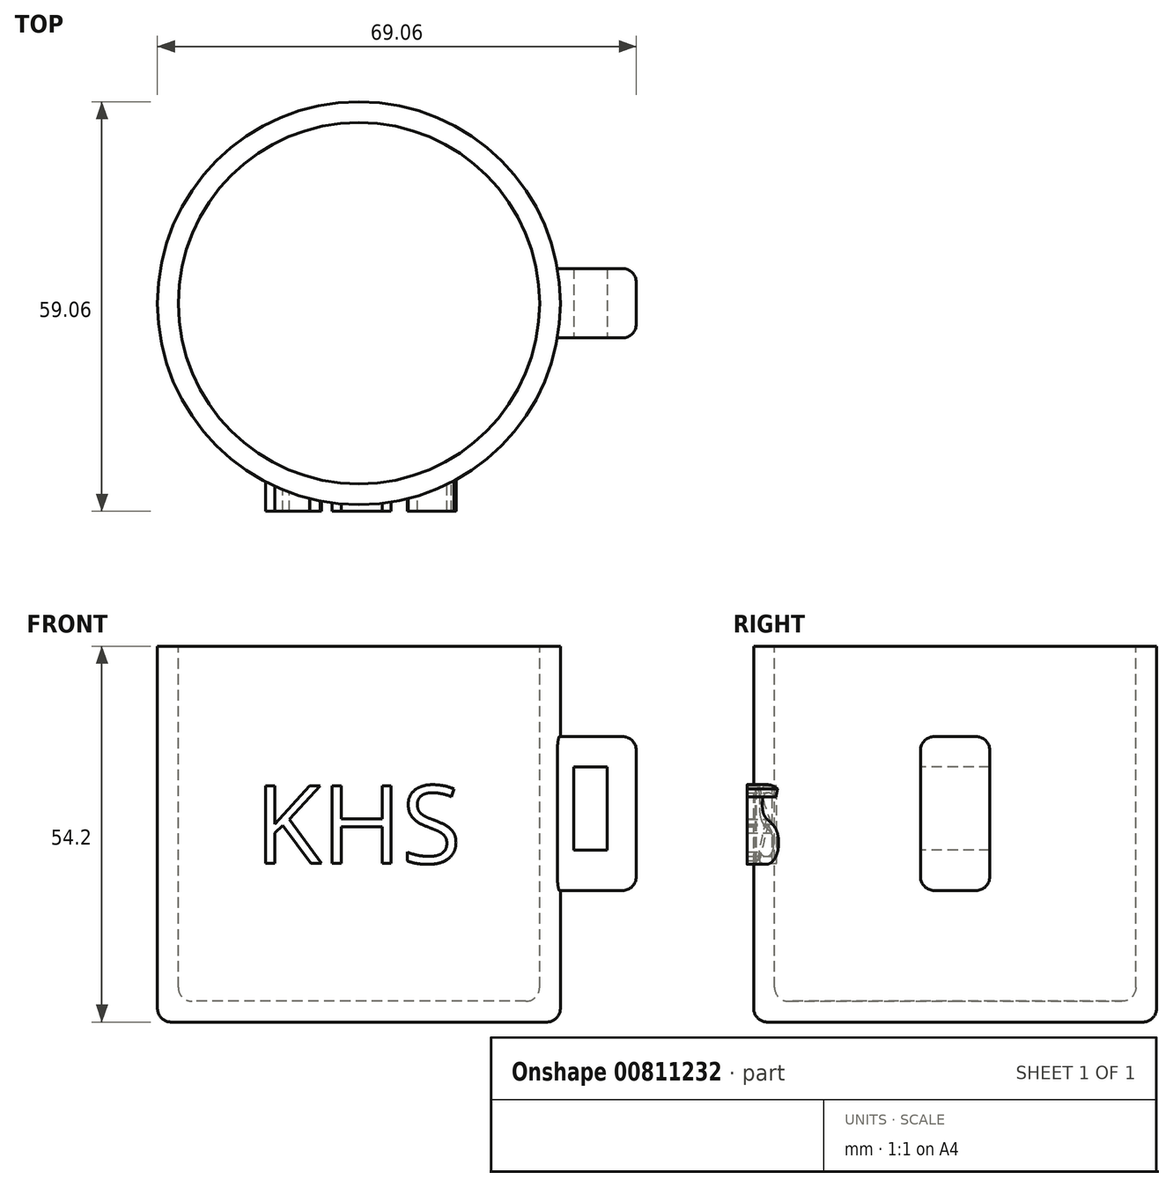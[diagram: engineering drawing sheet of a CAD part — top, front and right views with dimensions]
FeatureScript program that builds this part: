
annotation { "Feature Type Name" : "Feature", "Feature Type Description" : "" }
export const myFeature = defineFeature(function(context is Context, id is Id, definition is map)
    precondition{}
    {
        {
            var Q0;
            Q0=qCreatedBy(makeId("Front.planeOp"),FACE);
            var sketch = newSketch(context, id + "F0", { "sketchPlane" : qUnion([Q0])});
            skLineSegment(sketch, "E0", {"start": v(0, 41.97) * mm, "end": v(0, -44.14) * mm});
            skLineSegment(sketch, "E1", {"start": v(-6.15, -31.18) * mm, "end": v(24.06, -31.18) * mm});
            skLineSegment(sketch, "E2", {"start": v(26.06, -29.18) * mm, "end": v(26.06, 23.22) * mm});
            skLineSegment(sketch, "E3.0", {"start": v(29.06, -32.18) * mm, "end": v(29.06, 23.22) * mm});
            skLineSegment(sketch, "E3.1", {"start": v(-6.15, -34.18) * mm, "end": v(27.06, -34.18) * mm});
            skPoint(sketch, "E4.visualSharp", {"position": v(26.06, -31.18) * mm});
            skArc(sketch, "E4.filletArc", {"start": v(24.06, -31.18) * mm, "mid": v(25.48, -30.6) * mm, "end": v(26.06, -29.18) * mm});
            skPoint(sketch, "E5.visualSharp", {"position": v(29.06, -34.18) * mm});
            skArc(sketch, "E5.filletArc", {"start": v(27.06, -34.18) * mm, "mid": v(28.48, -33.6) * mm, "end": v(29.06, -32.18) * mm});
            skLineSegment(sketch, "E6", {"start": v(22.31, 20.02) * mm, "end": v(32.92, 20.02) * mm});
            skSolve(sketch);
        }
        {
            var Q0;
            {var subQ4=sQuery(id+"F0.wireOp",EDGE,"E4.filletArc");Q0=makeQuery(id+"F0.imprint","IMPRINT",FACE,{"disambiguationData":[TD([[makeQuery(id+"F0.imprint","IMPRINT",EDGE,{"derivedFrom":subQ4}),-1.0]])]});}
            var Q1;
            Q1=sQuery(id+"F0.wireOp",EDGE,"E0");
            revolve(context, id + "F1", {"surfaceOperationType" : NewSurfaceOperationType.NEW, "entities" : qUnion([Q0]), "axis" : qUnion([Q1]), "revolveType" : RevolveType.FULL});
        }
        {
            var Q0;
            Q0=qCreatedBy(makeId("Right.planeOp"),FACE);
            var sketch = newSketch(context, id + "F2", { "sketchPlane" : qUnion([Q0])});
            skLineSegment(sketch, "E7.bottom", {"start": v(-5, 7) * mm, "end": v(5, 7) * mm});
            skLineSegment(sketch, "E7.top", {"start": v(-5, -15.2) * mm, "end": v(5, -15.2) * mm});
            skLineSegment(sketch, "E7.left", {"start": v(-5, 7) * mm, "end": v(-5, -15.2) * mm});
            skLineSegment(sketch, "E7.right", {"start": v(5, 7) * mm, "end": v(5, -15.2) * mm});
            skSolve(sketch);
        }
        {
            var Q0;
            Q0=makeQuery(id+"F2.imprint","IMPRINT",FACE,{"disambiguationData":[TD([[makeQuery(id+"F2.imprint","IMPRINT",EDGE,{"derivedFrom":sQuery(id+"F2.wireOp",EDGE,"E7.bottom")}),-1.0]])]});
            extrude(context, id + "F3", {"entities" : qUnion([Q0]), "operationType" : NewBodyOperationType.ADD, "depth" : 40 * mm, "offsetDistance" : 25 * mm});
        }
        {
            var Q0;
            {var subQ0=sQuery(id+"F2.wireOp",EDGE,"E7.left");var subQ1=sQuery(id+"F2.wireOp",EDGE,"E7.bottom");Q0=makeQuery(id+"F3.boolean.opBoolean","SPLIT",EDGE,{"disambiguationData":[TD([makeQuery(id+"F1.opRevolve","SWEPT_FACE",FACE,{"disambiguationData":[OSD([sQuery(id+"F0.wireOp",EDGE,"E3.0")])]})])],"derivedFrom":makeQuery(id+"F3.opExtrude","SWEPT_EDGE",EDGE,{"disambiguationData":[OSD([subQ1,subQ0])]})});}
            var Q1;
            Q1=makeQuery(id+"F3.opExtrude","CAP_EDGE",EDGE,{"disambiguationData":[OSD([sQuery(id+"F2.wireOp",EDGE,"E7.bottom")])],"isStart":false});
            var Q2;
            Q2=makeQuery(id+"F3.opExtrude","CAP_EDGE",EDGE,{"disambiguationData":[OSD([sQuery(id+"F2.wireOp",EDGE,"E7.left")])],"isStart":false});
            var Q3;
            {var subQ0=sQuery(id+"F2.wireOp",EDGE,"E7.left");var subQ1=sQuery(id+"F2.wireOp",EDGE,"E7.top");Q3=makeQuery(id+"F3.boolean.opBoolean","SPLIT",EDGE,{"disambiguationData":[TD([makeQuery(id+"F1.opRevolve","SWEPT_FACE",FACE,{"disambiguationData":[OSD([sQuery(id+"F0.wireOp",EDGE,"E3.0")])]})])],"derivedFrom":makeQuery(id+"F3.opExtrude","SWEPT_EDGE",EDGE,{"disambiguationData":[OSD([subQ1,subQ0])]})});}
            var Q4;
            Q4=makeQuery(id+"F3.opExtrude","CAP_EDGE",EDGE,{"disambiguationData":[OSD([sQuery(id+"F2.wireOp",EDGE,"E7.top")])],"isStart":false});
            var Q5;
            Q5=makeQuery(id+"F3.opExtrude","CAP_EDGE",EDGE,{"disambiguationData":[OSD([sQuery(id+"F2.wireOp",EDGE,"E7.right")])],"isStart":false});
            var Q6;
            {var subQ0=sQuery(id+"F2.wireOp",EDGE,"E7.bottom");var subQ1=sQuery(id+"F2.wireOp",EDGE,"E7.right");Q6=makeQuery(id+"F3.boolean.opBoolean","SPLIT",EDGE,{"disambiguationData":[TD([makeQuery(id+"F1.opRevolve","SWEPT_FACE",FACE,{"disambiguationData":[OSD([sQuery(id+"F0.wireOp",EDGE,"E3.0")])]})])],"derivedFrom":makeQuery(id+"F3.opExtrude","SWEPT_EDGE",EDGE,{"disambiguationData":[OSD([subQ0,subQ1])]})});}
            var Q7;
            {var subQ0=sQuery(id+"F2.wireOp",EDGE,"E7.right");var subQ1=sQuery(id+"F2.wireOp",EDGE,"E7.top");Q7=makeQuery(id+"F3.boolean.opBoolean","SPLIT",EDGE,{"disambiguationData":[TD([makeQuery(id+"F1.opRevolve","SWEPT_FACE",FACE,{"disambiguationData":[OSD([sQuery(id+"F0.wireOp",EDGE,"E3.0")])]})])],"derivedFrom":makeQuery(id+"F3.opExtrude","SWEPT_EDGE",EDGE,{"disambiguationData":[OSD([subQ1,subQ0])]})});}
            fillet(context, id + "F4", {"entities" : qUnion([Q0, Q1, Q2, Q3, Q4, Q5, Q6, Q7]), "radius" : 2 * mm, "tangentPropagation" : true, "allowEdgeOverflow" : false});
        }
        {
            var Q0;
            {var subQ1=sQuery(id+"F2.wireOp",EDGE,"E7.left");Q0=makeQuery(id+"F3.boolean.opBoolean","SPLIT",FACE,{"disambiguationData":[TD([makeQuery(id+"F1.opRevolve","SWEPT_FACE",FACE,{"disambiguationData":[OSD([sQuery(id+"F0.wireOp",EDGE,"E3.0")])]})])],"derivedFrom":makeQuery(id+"F3.opExtrude","SWEPT_FACE",FACE,{"disambiguationData":[OSD([subQ1])]})});}
            var sketch = newSketch(context, id + "F5", { "sketchPlane" : qUnion([Q0])});
            skLineSegment(sketch, "E8.bottom", {"start": v(31, 2.65) * mm, "end": v(35.82, 2.65) * mm});
            skLineSegment(sketch, "E8.top", {"start": v(31, -9.4) * mm, "end": v(35.82, -9.4) * mm});
            skLineSegment(sketch, "E8.left", {"start": v(31, 2.65) * mm, "end": v(31, -9.4) * mm});
            skLineSegment(sketch, "E8.right", {"start": v(35.82, 2.65) * mm, "end": v(35.82, -9.4) * mm});
            skSolve(sketch);
        }
        {
            var Q0;
            Q0 = qSketchRegion(id + "F5", true);
            extrude(context, id + "F6", {"entities" : qUnion([Q0]), "operationType" : NewBodyOperationType.REMOVE, "oppositeDirection" : true, "depth" : 25 * mm, "offsetDistance" : 25 * mm});
        }
        {
            var Q0;
            Q0=qCreatedBy(makeId("Right.planeOp"),FACE);
            var sketch = newSketch(context, id + "F7", { "sketchPlane" : qUnion([Q0])});
            skLineSegment(sketch, "E9.bottom", {"start": v(-8.08, 9.89) * mm, "end": v(8.08, 9.89) * mm});
            skLineSegment(sketch, "E9.top", {"start": v(-8.08, -19.54) * mm, "end": v(8.08, -19.54) * mm});
            skLineSegment(sketch, "E9.left", {"start": v(-8.08, 9.89) * mm, "end": v(-8.08, -19.54) * mm});
            skLineSegment(sketch, "E9.right", {"start": v(8.08, 9.89) * mm, "end": v(8.08, -19.54) * mm});
            skSolve(sketch);
        }
        {
            var Q0;
            Q0 = qSketchRegion(id + "F7", true);
            var Q1;
            Q1=makeQuery(id+"F1.opRevolve","SWEPT_FACE",FACE,{"disambiguationData":[OSD([sQuery(id+"F0.wireOp",EDGE,"E2")])]});
            extrude(context, id + "F8", {"entities" : qUnion([Q0]), "operationType" : NewBodyOperationType.REMOVE, "endBound" : BoundingType.UP_TO_SURFACE, "depth" : 25 * mm, "endBoundEntityFace" : qUnion([Q1]), "offsetDistance" : 25 * mm});
        }
        {
            var Q0;
            Q0=qCreatedBy(makeId("Front.planeOp"),FACE);
            var sketch = newSketch(context, id + "F9", { "sketchPlane" : qUnion([Q0])});
            skText(sketch, "E10", { "text": "KHS", "fontName": "OpenSans-Regular.ttf"});
            const initialGuessF9  = {"E10": [-0.015, -0.01127, 1, 0, 0.01127]};
            skSetInitialGuess(sketch, initialGuessF9);
            skSolve(sketch);
        }
        {
            var Q0;
            Q0 = qSketchRegion(id + "F9", true);
            extrude(context, id + "F10", {"entities" : qUnion([Q0]), "operationType" : NewBodyOperationType.ADD, "depth" : 30 * mm, "offsetDistance" : 25 * mm});
        }
        {
            var Q0;
            Q0 = qSketchRegion(id + "F9", true);
            var Q1;
            {var subQ0=sQuery(id+"F0.wireOp",EDGE,"E2");Q1=makeQuery(id+"F8.boolean.opBoolean","MERGE",FACE,{"derivedFrom":[makeQuery(id+"F1.opRevolve","SWEPT_FACE",FACE,{"disambiguationData":[OSD([subQ0])]}),makeQuery(id+"F8.opExtrude","CAP_FACE",FACE,{"disambiguationData":[OSD([subQ0])],"isStart":false})]});}
            extrude(context, id + "F11", {"entities" : qUnion([Q0]), "operationType" : NewBodyOperationType.REMOVE, "endBound" : BoundingType.UP_TO_SURFACE, "depth" : 25 * mm, "endBoundEntityFace" : qUnion([Q1]), "offsetDistance" : 25 * mm});
        }
    });
